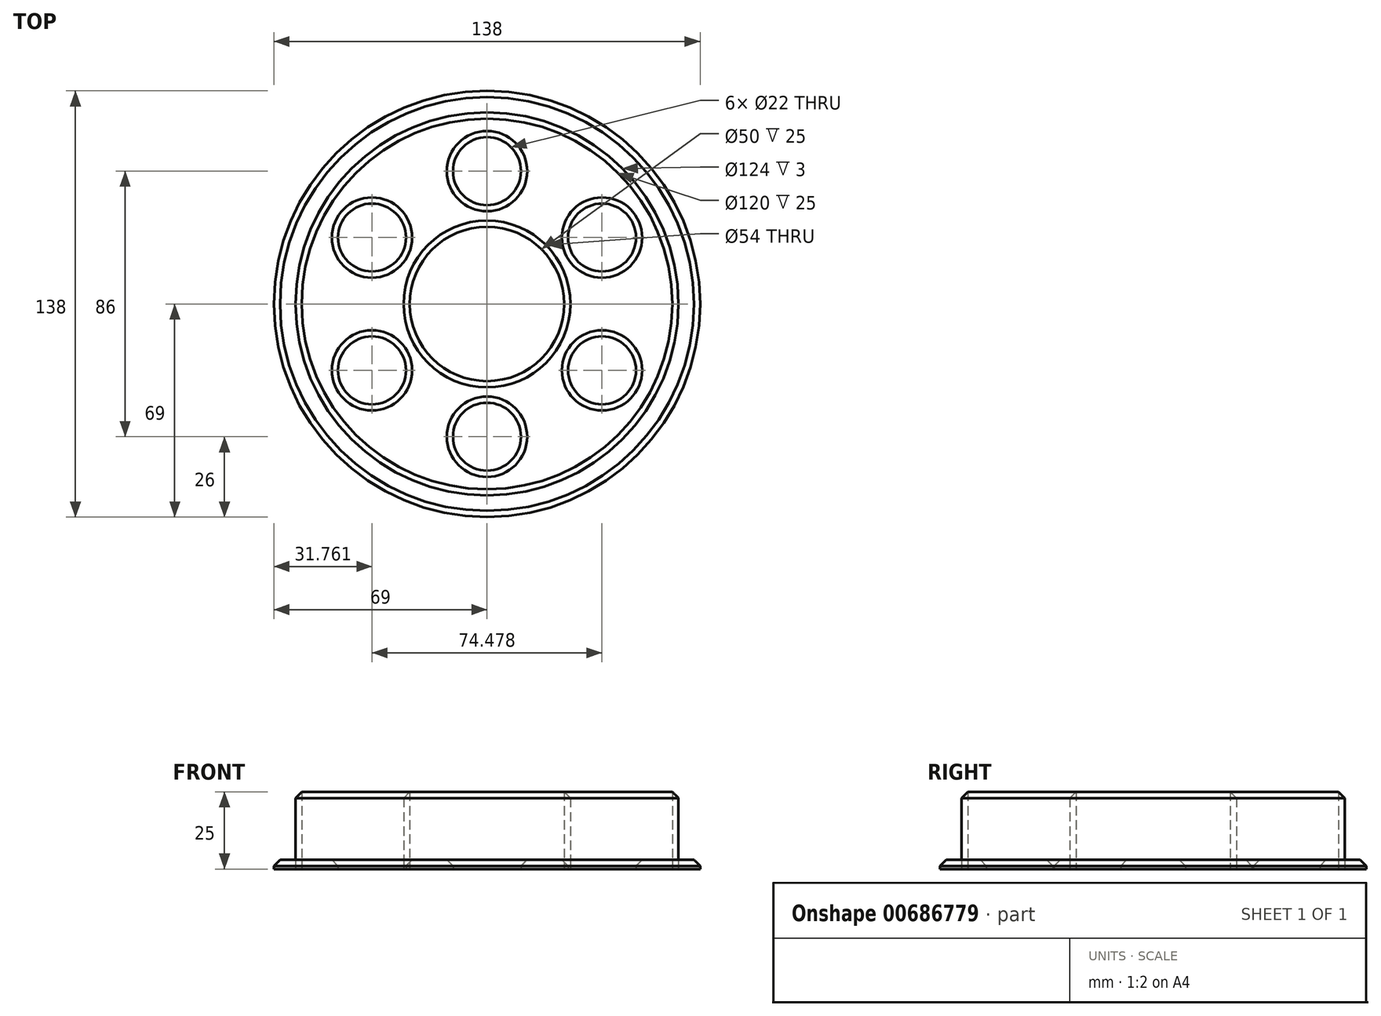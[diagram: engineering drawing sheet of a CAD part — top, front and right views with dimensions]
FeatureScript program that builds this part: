
annotation { "Feature Type Name" : "Feature", "Feature Type Description" : "" }
export const myFeature = defineFeature(function(context is Context, id is Id, definition is map)
    precondition{}
    {
        {
            var Q0;
            Q0=qCreatedBy(makeId("Top.planeOp"),FACE);
            var sketch = newSketch(context, id + "F0", { "sketchPlane" : qUnion([Q0])});
            skCircle(sketch, "E0", {"center": v(0, 0) * mm, "radius": 60 * mm});
            skCircle(sketch, "E1.0", {"center": v(0, 0) * mm, "radius": 62 * mm});
            skCircle(sketch, "E2.0", {"center": v(0, 0) * mm, "radius": 69 * mm});
            skCircle(sketch, "E3.0", {"center": v(0, 0) * mm, "radius": 54 * mm, "construction": true});
            skCircle(sketch, "E4", {"center": v(0, 0) * mm, "radius": 25 * mm});
            skCircle(sketch, "E5.0", {"center": v(0, 0) * mm, "radius": 27 * mm});
            skCircle(sketch, "E6.0", {"center": v(0, 0) * mm, "radius": 32 * mm, "construction": true});
            skCircle(sketch, "E7", {"center": v(0, 43) * mm, "radius": 11 * mm});
            skCircle(sketch, "E8.1.0", {"center": v(-37.24, 21.5) * mm, "radius": 11 * mm});
            skCircle(sketch, "E8.2.0", {"center": v(-37.24, -21.5) * mm, "radius": 11 * mm});
            skCircle(sketch, "E8.3.0", {"center": v(0, -43) * mm, "radius": 11 * mm});
            skCircle(sketch, "E8.4.0", {"center": v(37.24, -21.5) * mm, "radius": 11 * mm});
            skCircle(sketch, "E8.5.0", {"center": v(37.24, 21.5) * mm, "radius": 11 * mm});
            skSolve(sketch);
        }
        {
            var Q0;
            Q0=makeQuery(id+"F0.imprint","IMPRINT",FACE,{"disambiguationData":[TD([[makeQuery(id+"F0.imprint","IMPRINT",EDGE,{"derivedFrom":sQuery(id+"F0.wireOp",EDGE,"E1.0")}),-1.0]])]});
            var Q1;
            Q1=makeQuery(id+"F0.imprint","IMPRINT",FACE,{"disambiguationData":[TD([[makeQuery(id+"F0.imprint","IMPRINT",EDGE,{"derivedFrom":sQuery(id+"F0.wireOp",EDGE,"E0")}),1.0]])]});
            extrude(context, id + "F1", {"entities" : qUnion([Q0, Q1]), "depth" : 3 * mm, "offsetDistance" : 25 * mm});
        }
        {
            var Q0;
            Q0=makeQuery(id+"F0.imprint","IMPRINT",FACE,{"disambiguationData":[TD([[makeQuery(id+"F0.imprint","IMPRINT",EDGE,{"derivedFrom":sQuery(id+"F0.wireOp",EDGE,"E0")}),-1.0]])]});
            var Q1;
            Q1=makeQuery(id+"F0.imprint","IMPRINT",FACE,{"disambiguationData":[TD([[makeQuery(id+"F0.imprint","IMPRINT",EDGE,{"derivedFrom":sQuery(id+"F0.wireOp",EDGE,"E4")}),-1.0]])]});
            extrude(context, id + "F2", {"entities" : qUnion([Q0, Q1]), "depth" : 25 * mm, "offsetDistance" : 25 * mm});
        }
        {
            var Q0;
            Q0=makeQuery(id+"F2.opExtrude","CAP_EDGE",EDGE,{"disambiguationData":[OSD([sQuery(id+"F0.wireOp",EDGE,"E1.0")])],"isStart":false});
            chamfer(context, id + "F3", {"entities" : qUnion([Q0]), "width" : 2 * mm, "tangentPropagation" : true});
        }
        {
            var Q0;
            Q0=makeQuery(id+"F1.opExtrude","CAP_EDGE",EDGE,{"disambiguationData":[OSD([sQuery(id+"F0.wireOp",EDGE,"E2.0")])],"isStart":false});
            chamfer(context, id + "F4", {"entities" : qUnion([Q0]), "width" : 2 * mm, "tangentPropagation" : true});
        }
        {
            var Q0;
            Q0=makeQuery(id+"F2.opExtrude","CAP_EDGE",EDGE,{"disambiguationData":[OSD([sQuery(id+"F0.wireOp",EDGE,"E5.0")])],"isStart":false});
            chamfer(context, id + "F5", {"entities" : qUnion([Q0]), "width" : 2 * mm, "tangentPropagation" : true});
        }
        {
            var Q0;
            Q0=makeQuery(id+"F1.opExtrude","CAP_EDGE",EDGE,{"disambiguationData":[OSD([sQuery(id+"F0.wireOp",EDGE,"E8.2.0")])],"isStart":false});
            var Q1;
            Q1=makeQuery(id+"F1.opExtrude","CAP_EDGE",EDGE,{"disambiguationData":[OSD([sQuery(id+"F0.wireOp",EDGE,"E8.1.0")])],"isStart":false});
            var Q2;
            Q2=makeQuery(id+"F1.opExtrude","CAP_EDGE",EDGE,{"disambiguationData":[OSD([sQuery(id+"F0.wireOp",EDGE,"E7")])],"isStart":false});
            var Q3;
            Q3=makeQuery(id+"F1.opExtrude","CAP_EDGE",EDGE,{"disambiguationData":[OSD([sQuery(id+"F0.wireOp",EDGE,"E8.5.0")])],"isStart":false});
            var Q4;
            Q4=makeQuery(id+"F1.opExtrude","CAP_EDGE",EDGE,{"disambiguationData":[OSD([sQuery(id+"F0.wireOp",EDGE,"E8.4.0")])],"isStart":false});
            var Q5;
            Q5=makeQuery(id+"F1.opExtrude","CAP_EDGE",EDGE,{"disambiguationData":[OSD([sQuery(id+"F0.wireOp",EDGE,"E8.3.0")])],"isStart":false});
            chamfer(context, id + "F6", {"entities" : qUnion([Q0, Q1, Q2, Q3, Q4, Q5]), "width" : 2 * mm, "tangentPropagation" : true});
        }
    });
